# Revit family: QF_ELECTROLUXPROFESSIONAL_1LSNC5_IC64832_G
name_source: partatom
category: Attrezzature speciali
units: mm (PartAtom-declared; Revit-internal decimal feet)

## family parameters
Basato su piano di lavoro = No
Condiviso = No
Punto di calcolo locali = No
Quota connettore circolare = Usa diametro
Sempre verticale = Sì
Taglio con vuoti quando caricato = No
Tipo di parte = Normale

## types (10) — shared parameters
Depth Actual = 1110 mm
Gas KW = 65
Height Actual = 1270 mm  [stored 4.16667 ft]
Latent Heat Output = 0.0
Length Actual = 3835 mm
Modello = IC64832
Phase = 3
Produttore = Electrolux Professional
Sensible Heat Output = 0.0
URL = www.electroluxprofessional.com
Weight = 1040
zero-valued in all types: Prospetto di default, Steam Pounds per Hour

## per-type parameters (varying)
| type | Cycle | Descrizione | Item Number | Volts | Watts |
| 9882030116 | 50 Hz | IRONER CYLINDER IC64832 3170MM PERFORMANCE GAS CE 400/50/3 DUBIXIUM FR VAC.FEED.TABLE | 1L0GMG | 400 V | 3200 W |
| 9882030240 | 60 Hz | IRONER CYLINDER IC64832 3170MM ACTIVE GAS CE 400/60/3 6MM SST CYL. EN, ES, PO FEED NOW | 1LSPHX | 400 V | 3200 W |
| 9882030210 | 60 Hz | IRONER CYLINDER IC64832 3170MM ACTIVE GAS CE 208-240/60/3 6MM SST CYL. EN, ES, PO FEED NOW | 1L8278 | 240 V | 2000 W |
| 9882030198 | 50 Hz | IRONER CYLINDER IC64832 3170MM ACTIVE GAS CE 400/50/3 6MM SST CYL. FR FEED NOW | 1L826X | 400 V | 3200 W |
| 9882030117 | 50 Hz | IRONER CYLINDER IC64832 3170MM SUPERIOR GAS CE 400/50/3 DUBIXIUM FR FEED ALONE VAC.FEED.TABLE | 1L0GMH | 400 V | 3200 W |
| 9882030132 | 50 Hz | IRONER CYLINDER IC64832 3170MM PERFORMANCE GAS CE 400/50/3 DUBIXIUM ML VAC.FEED.TABLE | 1L0GMZ | 400 V | 3200 W |
| 9882030221 | 50 Hz | IRONER CYLINDER IC64832 3170MM GAS CE 400/50/3 DUBIXIUM ML VAC.FEED.TABLE DIAMMS | 1L0GUJ | 400 V | 3200 W |
| 9882030133 | 50 Hz | IRONER CYLINDER IC64832 3170MM SUPERIOR GAS CE 400/50/3 DUBIXIUM ML FEED ALONE VAC.FEED.TABLE | 1L0GN0 | 400 V | 3200 W |
| 9882030202 | 50 Hz | IRONER CYLINDER IC64832 3170MM ACTIVE GAS CE 400/50/3 6MM SST CYL. ML FEED NOW | 1L8271 | 400 V | 3200 W |
| 9882030037 | 50 Hz | IRONER CYLINDER IC64832 3170MM GAS CE 400/50/3 6MM SST CYL. FR FEED NOW FEED ALONE VAC.FEED.TABLE | 1LSP03 | 400 V | 3200 W |

note: [stored X ft] marks values corroborated as IEEE doubles in the binary element streams (Revit-internal decimal feet)

## geometry (parser evidence)
native form markers: Sweep x8
no freeform markers — native parametric forms only
